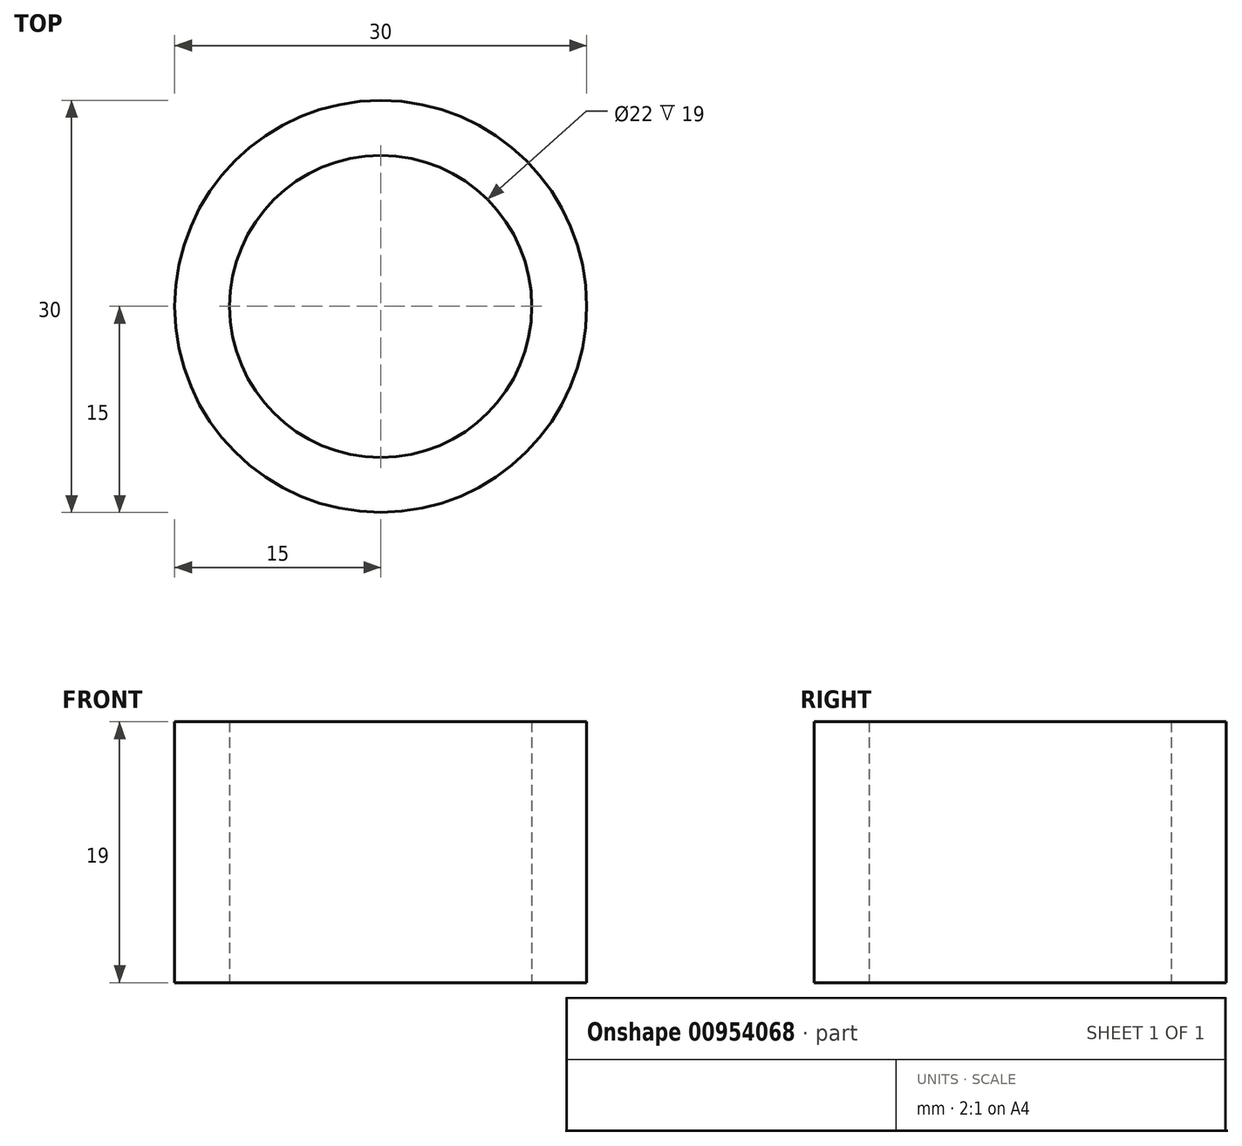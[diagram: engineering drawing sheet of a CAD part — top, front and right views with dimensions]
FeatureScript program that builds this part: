
annotation { "Feature Type Name" : "Feature", "Feature Type Description" : "" }
export const myFeature = defineFeature(function(context is Context, id is Id, definition is map)
    precondition{}
    {
        {
            var Q0;
            Q0=qCreatedBy(makeId("Top.planeOp"),FACE);
            var sketch = newSketch(context, id + "F0", { "sketchPlane" : qUnion([Q0])});
            skCircle(sketch, "E0", {"center": v(0, 0) * mm, "radius": 11 * mm});
            skCircle(sketch, "E1", {"center": v(0, 0) * mm, "radius": 15 * mm});
            skSolve(sketch);
        }
        {
            var Q0;
            Q0=makeQuery(id+"F0.imprint","IMPRINT",FACE,{"disambiguationData":[TD([[makeQuery(id+"F0.imprint","IMPRINT",EDGE,{"derivedFrom":sQuery(id+"F0.wireOp",EDGE,"E0")}),-1.0]])]});
            extrude(context, id + "F1", {"entities" : qUnion([Q0]), "depth" : 19 * mm, "offsetDistance" : 25 * mm});
        }
    });
